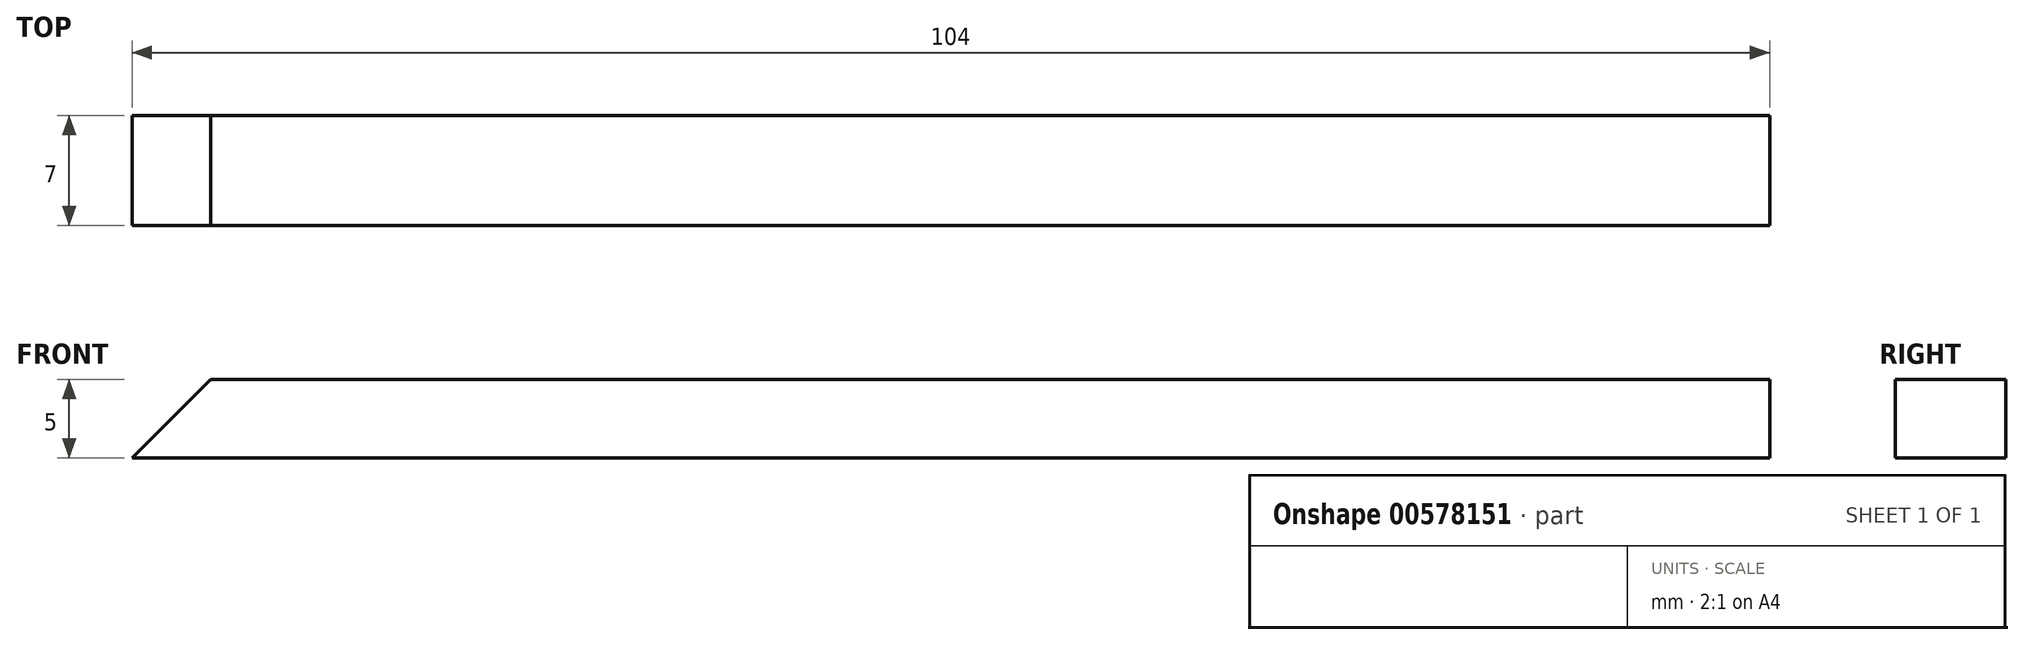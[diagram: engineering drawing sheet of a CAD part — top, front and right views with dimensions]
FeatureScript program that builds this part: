
annotation { "Feature Type Name" : "Feature", "Feature Type Description" : "" }
export const myFeature = defineFeature(function(context is Context, id is Id, definition is map)
    precondition{}
    {
        {
            var Q0;
            Q0=qCreatedBy(makeId("Top.planeOp"),FACE);
            var sketch = newSketch(context, id + "F0", { "sketchPlane" : qUnion([Q0])});
            skLineSegment(sketch, "E0.bottom", {"start": v(40, -3.5) * mm, "end": v(-40, -3.5) * mm});
            skLineSegment(sketch, "E0.top", {"start": v(40, 3.5) * mm, "end": v(-40, 3.5) * mm});
            skLineSegment(sketch, "E0.left", {"start": v(40, -3.5) * mm, "end": v(40, 3.5) * mm});
            skLineSegment(sketch, "E0.right", {"start": v(-40, -3.5) * mm, "end": v(-40, 3.5) * mm});
            skPoint(sketch, "E0.middle", {"position": v(0, 0) * mm});
            skLineSegment(sketch, "E1.bottom", {"start": v(-40, 3.5) * mm, "end": v(-49, 3.5) * mm});
            skLineSegment(sketch, "E1.top", {"start": v(-40, -3.5) * mm, "end": v(-49, -3.5) * mm});
            skLineSegment(sketch, "E1.left", {"start": v(-40, 3.5) * mm, "end": v(-40, -3.5) * mm});
            skLineSegment(sketch, "E1.right", {"start": v(-49, 3.5) * mm, "end": v(-49, -3.5) * mm});
            skLineSegment(sketch, "E2.top", {"start": v(40, -3.5) * mm, "end": v(55, -3.5) * mm});
            skLineSegment(sketch, "E2.left", {"start": v(40, 3.5) * mm, "end": v(40, -3.5) * mm});
            skLineSegment(sketch, "E2.right", {"start": v(55, 3.5) * mm, "end": v(55, -3.5) * mm});
            skLineSegment(sketch, "E3", {"start": v(40, 3.5) * mm, "end": v(55, 3.5) * mm});
            skSolve(sketch);
        }
        {
            var Q0;
            Q0=makeQuery(id+"F0.imprint","IMPRINT",FACE,{"disambiguationData":[TD([[makeQuery(id+"F0.imprint","IMPRINT",EDGE,{"derivedFrom":sQuery(id+"F0.wireOp",EDGE,"E1.bottom")}),1.0]])]});
            var Q1;
            Q1=makeQuery(id+"F0.imprint","IMPRINT",FACE,{"disambiguationData":[TD([[makeQuery(id+"F0.imprint","IMPRINT",EDGE,{"derivedFrom":sQuery(id+"F0.wireOp",EDGE,"E0.bottom")}),-1.0]])]});
            var Q2;
            Q2=makeQuery(id+"F0.imprint","IMPRINT",FACE,{"disambiguationData":[TD([[makeQuery(id+"F0.imprint","IMPRINT",EDGE,{"derivedFrom":sQuery(id+"F0.wireOp",EDGE,"E2.top")}),1.0]])]});
            extrude(context, id + "F1", {"entities" : qUnion([Q0, Q1, Q2]), "depth" : 5 * mm, "offsetDistance" : 25 * mm});
        }
        {
            var Q0;
            Q0=makeQuery(id+"F1.opExtrude","SWEPT_FACE",FACE,{"disambiguationData":[OSD([sQuery(id+"F0.wireOp",EDGE,"E0.bottom"),sQuery(id+"F0.wireOp",EDGE,"E1.top"),sQuery(id+"F0.wireOp",EDGE,"E2.top")])]});
            var sketch = newSketch(context, id + "F2", { "sketchPlane" : qUnion([Q0])});
            skLineSegment(sketch, "E4.bottom", {"start": v(-49, 5) * mm, "end": v(-44, 5) * mm});
            skLineSegment(sketch, "E4.top", {"start": v(-49, 0) * mm, "end": v(-44, 0) * mm});
            skLineSegment(sketch, "E4.left", {"start": v(-49, 5) * mm, "end": v(-49, 0) * mm});
            skLineSegment(sketch, "E4.right", {"start": v(-44, 5) * mm, "end": v(-44, 0) * mm});
            skLineSegment(sketch, "E5", {"start": v(-49, 0) * mm, "end": v(-44, 5) * mm});
            skSolve(sketch);
        }
        {
            var Q0;
            Q0=makeQuery(id+"F2.imprint","IMPRINT",FACE,{"disambiguationData":[TD([[makeQuery(id+"F2.imprint","IMPRINT",EDGE,{"derivedFrom":sQuery(id+"F2.wireOp",EDGE,"E4.bottom")}),1.0]])]});
            extrude(context, id + "F3", {"entities" : qUnion([Q0]), "operationType" : NewBodyOperationType.REMOVE, "oppositeDirection" : true, "depth" : 7 * mm, "offsetDistance" : 25 * mm});
        }
    });
